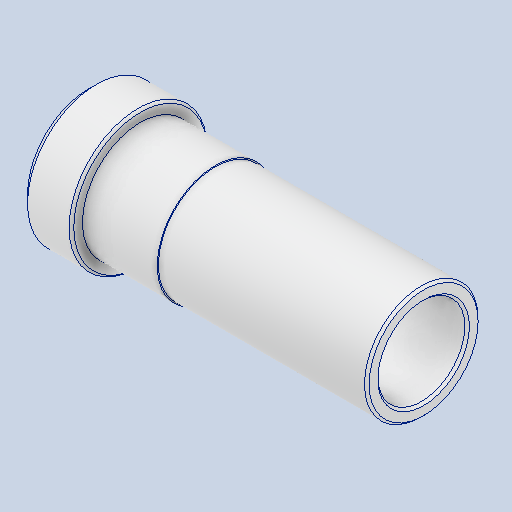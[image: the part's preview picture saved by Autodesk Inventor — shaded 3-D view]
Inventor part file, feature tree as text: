
AUTODESK INVENTOR PART (.ipt)
format: ipt  version: 2024 (Build 280153000, 153)  size: 144,896 bytes
history: native  units: in
note: dims shown in document units (in); Inventor stores cm internally (conversion verified against a paired STEP export)
features: chamfer x1
ambient origin geometry x8: Origin, YZ Plane, XZ Plane, XY Plane, X Axis, Y Axis, Z Axis, Center Point
bodies: Solid1 (feature_tree)
feature tree (1):
  chamfer  "Chamfer3"  [1 undecoded]
note: 1 required parameter value undecoded (feature->parameter linkage not recoverable at this tier; creation-order binding heuristic only, values carry confidence <= 0.55)
